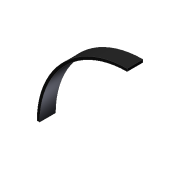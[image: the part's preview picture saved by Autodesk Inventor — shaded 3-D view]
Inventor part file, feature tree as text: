
AUTODESK INVENTOR PART (.ipt)
format: ipt  version: 2012 (Build 160160000, 160)  size: 72,192 bytes
history: native  units: in
note: dims shown in document units (in); Inventor stores cm internally (conversion verified against a paired STEP export)
features: extrude x1, sketch x1
ambient origin geometry x8: Origin, YZ Plane, XZ Plane, XY Plane, X Axis, Y Axis, Z Axis, Center Point
bodies: Solid1 (feature_tree)
feature tree (2):
  extrude  "Extrusion1"  Depth=0.25in
  sketch  "Sketch1"  dims[d0=8.25in d1=0.25in d2=1.5in d3=0.0in]
